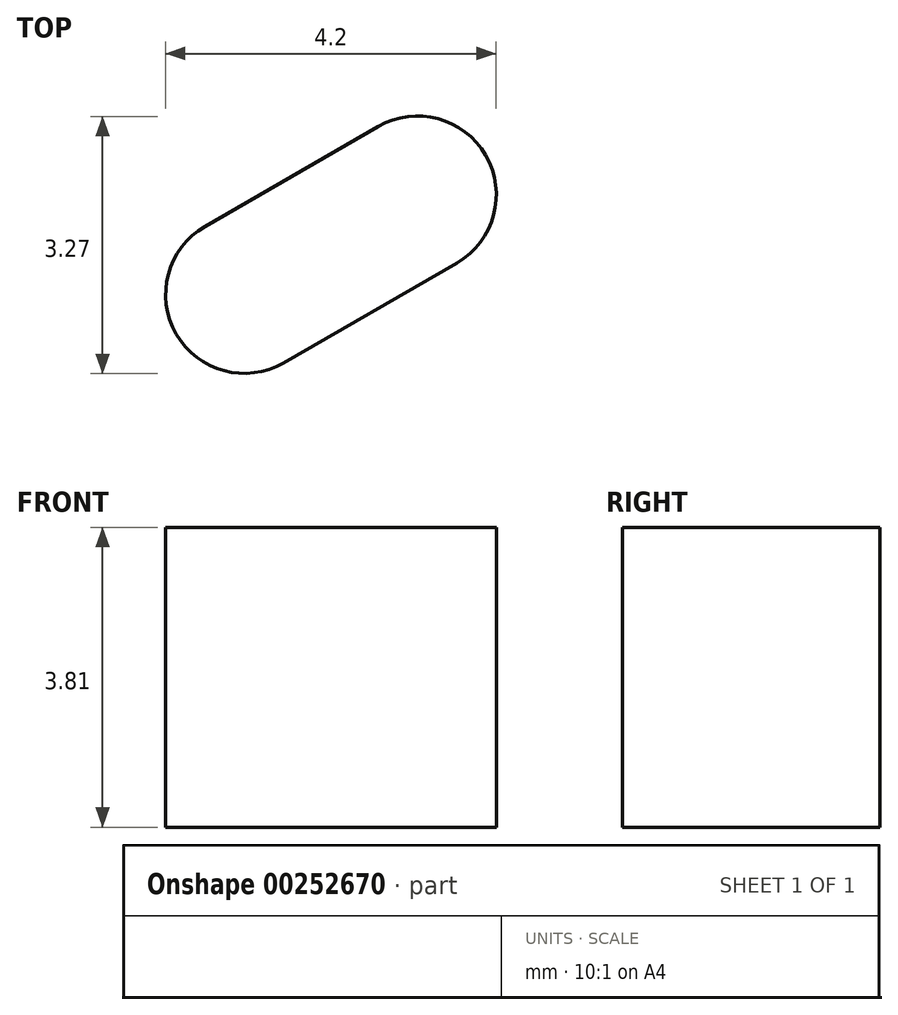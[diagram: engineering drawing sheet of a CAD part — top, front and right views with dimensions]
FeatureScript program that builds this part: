
annotation { "Feature Type Name" : "Feature", "Feature Type Description" : "" }
export const myFeature = defineFeature(function(context is Context, id is Id, definition is map)
    precondition{}
    {
        {
            var Q0;
            Q0=qCreatedBy(makeId("Top.planeOp"),FACE);
            var sketch = newSketch(context, id + "F0", { "sketchPlane" : qUnion([Q0])});
            skCircle(sketch, "E0", {"center": v(0, 0) * mm, "radius": 16.51 * mm, "construction": true});
            skLineSegment(sketch, "E1", {"start": v(-14.3, -8.25) * mm, "end": v(-16.5, -9.52) * mm, "construction": true});
            skLineSegment(sketch, "E2", {"start": v(10.16, -13.01) * mm, "end": v(11.73, -15.01) * mm, "construction": true});
            skCircle(sketch, "E3", {"center": v(0, 0) * mm, "radius": 19.05 * mm, "construction": true});
            skLineSegment(sketch, "E4", {"start": v(0, 16.51) * mm, "end": v(0, 19.05) * mm, "construction": true});
            skArc(sketch, "E5.0.startCap", {"start": v(-14.8, -7.39) * mm, "mid": v(-13.43, -7.75) * mm, "end": v(-13.8, -9.12) * mm});
            skArc(sketch, "E5.0.endCap", {"start": v(-16, -10.4) * mm, "mid": v(-17.36, -10.02) * mm, "end": v(-17, -8.66) * mm});
            skLineSegment(sketch, "E5.0.left", {"start": v(-13.8, -9.12) * mm, "end": v(-16, -10.4) * mm});
            skLineSegment(sketch, "E5.0.right", {"start": v(-14.8, -7.39) * mm, "end": v(-17, -8.66) * mm});
            skCircle(sketch, "E6", {"center": v(0, 0) * mm, "radius": 12.7 * mm});
            skCircle(sketch, "E7", {"center": v(0, 0) * mm, "radius": 22.23 * mm});
            skArc(sketch, "E8.0.startCap", {"start": v(1, 16.51) * mm, "mid": v(0, 15.51) * mm, "end": v(-1, 16.51) * mm});
            skArc(sketch, "E8.0.endCap", {"start": v(-1, 19.05) * mm, "mid": v(0, 20.05) * mm, "end": v(1, 19.05) * mm});
            skLineSegment(sketch, "E8.0.left", {"start": v(-1, 16.51) * mm, "end": v(-1, 19.05) * mm});
            skLineSegment(sketch, "E8.0.right", {"start": v(1, 16.51) * mm, "end": v(1, 19.05) * mm});
            skArc(sketch, "E8.1.startCap", {"start": v(9.38, -13.63) * mm, "mid": v(9.55, -12.22) * mm, "end": v(10.95, -12.4) * mm});
            skArc(sketch, "E8.1.endCap", {"start": v(12.52, -14.4) * mm, "mid": v(12.34, -15.8) * mm, "end": v(10.94, -15.63) * mm});
            skLineSegment(sketch, "E8.1.left", {"start": v(10.95, -12.4) * mm, "end": v(12.52, -14.4) * mm});
            skLineSegment(sketch, "E8.1.right", {"start": v(9.38, -13.63) * mm, "end": v(10.94, -15.63) * mm});
            skSolve(sketch);
        }
        {
            var Q0;
            Q0=makeQuery(id+"F0.imprint","IMPRINT",FACE,{"disambiguationData":[TD([[makeQuery(id+"F0.imprint","IMPRINT",EDGE,{"derivedFrom":sQuery(id+"F0.wireOp",EDGE,"E5.0.startCap")}),1.0]])]});
            extrude(context, id + "F1", {"entities" : qUnion([Q0]), "depth" : 3.8 * mm});
        }
    });
